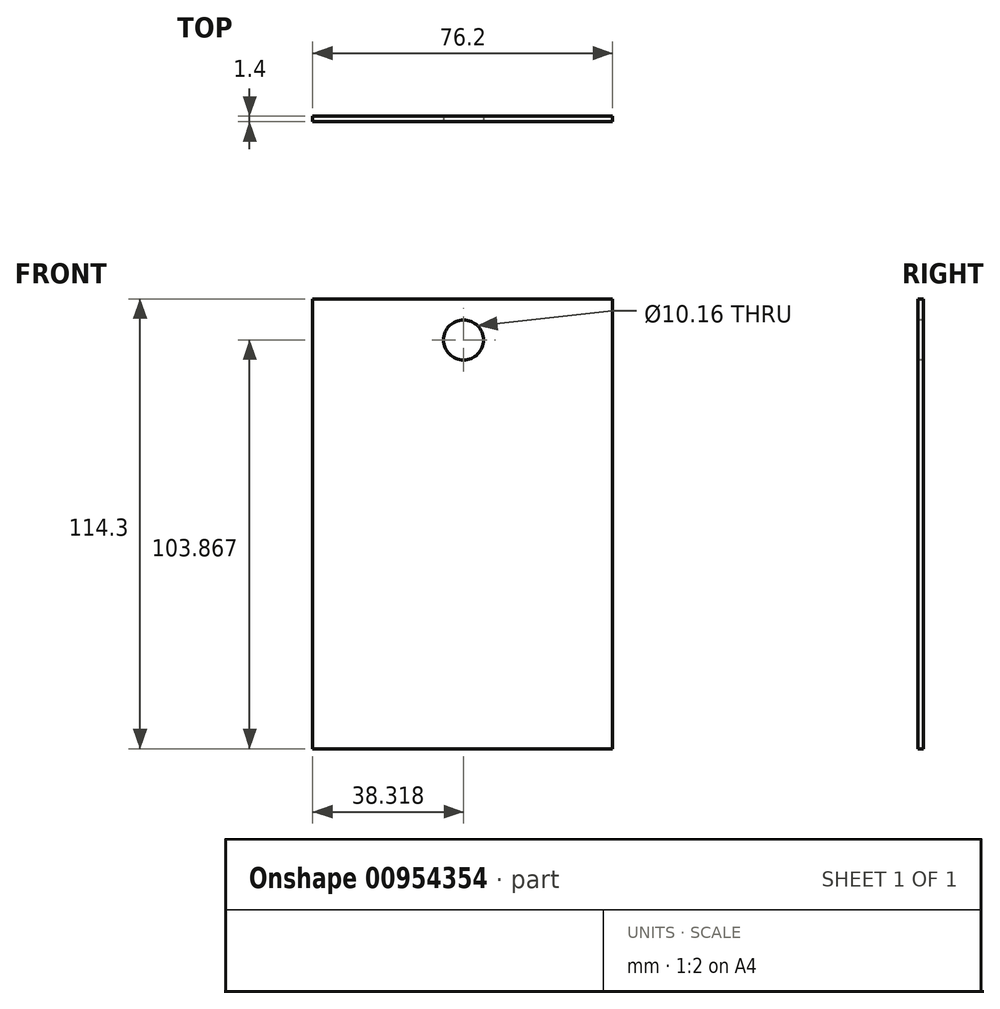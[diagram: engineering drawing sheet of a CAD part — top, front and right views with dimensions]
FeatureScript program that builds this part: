
annotation { "Feature Type Name" : "Feature", "Feature Type Description" : "" }
export const myFeature = defineFeature(function(context is Context, id is Id, definition is map)
    precondition{}
    {
        {
            var Q0;
            Q0=qCreatedBy(makeId("Front.planeOp"),FACE);
            var sketch = newSketch(context, id + "F0", { "sketchPlane" : qUnion([Q0])});
            skLineSegment(sketch, "E0.bottom", {"start": v(-255.86, 114.3) * mm, "end": v(-179.66, 114.3) * mm});
            skLineSegment(sketch, "E0.top", {"start": v(-255.86, 0) * mm, "end": v(-179.66, 0) * mm});
            skLineSegment(sketch, "E0.left", {"start": v(-255.86, 114.3) * mm, "end": v(-255.86, 0) * mm});
            skLineSegment(sketch, "E0.right", {"start": v(-179.66, 114.3) * mm, "end": v(-179.66, 0) * mm});
            skSolve(sketch);
        }
        {
            var Q0;
            Q0=makeQuery(id+"F0.imprint","IMPRINT",FACE,{"disambiguationData":[TD([[makeQuery(id+"F0.imprint","IMPRINT",EDGE,{"derivedFrom":sQuery(id+"F0.wireOp",EDGE,"E0.bottom")}),-1.0]])]});
            extrude(context, id + "F1", {"entities" : qUnion([Q0]), "depth" : 1.4 * mm, "offsetDistance" : 25.4 * mm});
        }
        {
            var Q0;
            Q0=makeQuery(id+"F1.opExtrude","CAP_FACE",FACE,{"disambiguationData":[OSD([sQuery(id+"F0.wireOp",EDGE,"E0.bottom"),sQuery(id+"F0.wireOp",EDGE,"E0.top"),sQuery(id+"F0.wireOp",EDGE,"E0.left"),sQuery(id+"F0.wireOp",EDGE,"E0.right")])],"isStart":false});
            var sketch = newSketch(context, id + "F2", { "sketchPlane" : qUnion([Q0])});
            skCircle(sketch, "E1", {"center": v(-217.54, 103.87) * mm, "radius": 4.05 * mm, "construction": true});
            skSolve(sketch);
        }
        {
            var Q0;
            Q0=sQuery(id+"F2.wireOp",VERTEX,"E1.center");
            var Q1;
            Q1=makeQuery(id+"F1.opExtrude","SWEPT_BODY",BODY,{"disambiguationData":[OSD([sQuery(id+"F0.wireOp",EDGE,"E0.bottom"),sQuery(id+"F0.wireOp",EDGE,"E0.top"),sQuery(id+"F0.wireOp",EDGE,"E0.left"),sQuery(id+"F0.wireOp",EDGE,"E0.right")])]});
            hole(context, id + "F3", {"style" : HoleStyle.SIMPLE, "endStyle" : HoleEndStyle.THROUGH, "holeDiameter" : 10.16 * mm, "majorDiameter" : 6.35 * mm, "isTappedThrough" : true, "tappedDepth" : 12.7 * mm, "tapClearance" : 3, "startFromSketch" : true, "locations" : qUnion([Q0]), "scope" : qUnion([Q1])});
        }
    });
